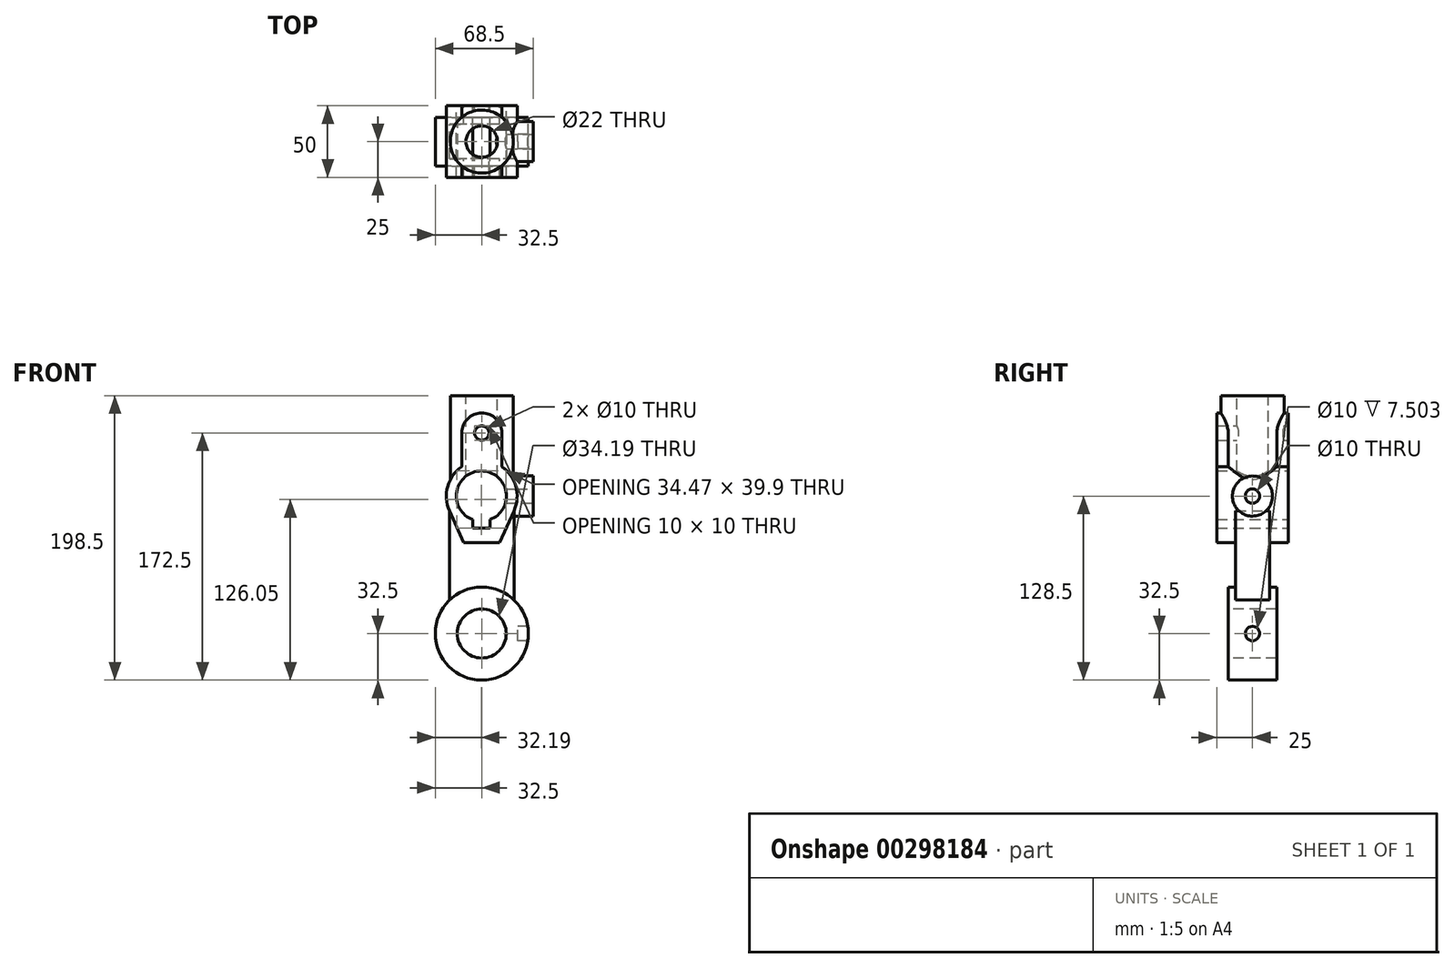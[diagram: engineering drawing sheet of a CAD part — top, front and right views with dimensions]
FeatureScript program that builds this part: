
annotation { "Feature Type Name" : "Feature", "Feature Type Description" : "" }
export const myFeature = defineFeature(function(context is Context, id is Id, definition is map)
    precondition{}
    {
        {
            var Q0;
            Q0=qCreatedBy(makeId("Front.planeOp"),FACE);
            var sketch = newSketch(context, id + "F0", { "sketchPlane" : qUnion([Q0])});
            skLineSegment(sketch, "E0.bottom", {"start": v(-22.5, 96) * mm, "end": v(22.5, 96) * mm});
            skLineSegment(sketch, "E0.top", {"start": v(-22.5, 0) * mm, "end": v(22.5, 0) * mm});
            skLineSegment(sketch, "E0.left", {"start": v(-22.5, 96) * mm, "end": v(-22.5, 0) * mm});
            skLineSegment(sketch, "E0.right", {"start": v(22.5, 96) * mm, "end": v(22.5, 0) * mm});
            skPoint(sketch, "E1", {"position": v(0, 0) * mm});
            skLineSegment(sketch, "E2", {"start": v(0, 0) * mm, "end": v(0, -10.14) * mm, "construction": true});
            skSolve(sketch);
        }
        {
            var Q0;
            Q0 = qSketchRegion(id + "F0", true);
            extrude(context, id + "F1", {"entities" : qUnion([Q0]), "endBound" : BoundingType.SYMMETRIC, "depth" : 24 * mm});
        }
        {
            var Q0;
            Q0=qCreatedBy(makeId("Front.planeOp"),FACE);
            var sketch = newSketch(context, id + "F2", { "sketchPlane" : qUnion([Q0])});
            skCircle(sketch, "E3", {"center": v(0, 0) * mm, "radius": 32.5 * mm});
            skSolve(sketch);
        }
        {
            var Q0;
            Q0 = qSketchRegion(id + "F2", true);
            extrude(context, id + "F3", {"entities" : qUnion([Q0]), "operationType" : NewBodyOperationType.ADD, "endBound" : BoundingType.SYMMETRIC, "depth" : 34 * mm});
        }
        {
            var Q0;
            Q0=qCreatedBy(makeId("Front.planeOp"),FACE);
            var sketch = newSketch(context, id + "F4", { "sketchPlane" : qUnion([Q0])});
            skLineSegment(sketch, "E4", {"start": v(-13.04, 100.57) * mm, "end": v(-13.04, 100.57) * mm});
            skLineSegment(sketch, "E5", {"start": v(0, 0) * mm, "end": v(-53.48, 0) * mm, "construction": true});
            skLineSegment(sketch, "E6", {"start": v(0, 100.39) * mm, "end": v(-0.3, 96) * mm, "construction": true});
            skCircle(sketch, "E7", {"center": v(0, 140) * mm, "radius": 5 * mm});
            skArc(sketch, "E8", {"start": v(-14, 140) * mm, "mid": v(0, 154) * mm, "end": v(14, 140) * mm});
            skArc(sketch, "E9", {"start": v(-6.3, 79.56) * mm, "mid": v(-0.3, 113.5) * mm, "end": v(5.7, 79.56) * mm});
            skLineSegment(sketch, "E10", {"start": v(-6.3, 79.56) * mm, "end": v(-6.3, 73.6) * mm});
            skLineSegment(sketch, "E11", {"start": v(-6.3, 73.6) * mm, "end": v(5.7, 73.6) * mm});
            skLineSegment(sketch, "E12", {"start": v(5.7, 73.6) * mm, "end": v(5.7, 79.56) * mm});
            skLineSegment(sketch, "E13", {"start": v(-12.5, 63.6) * mm, "end": v(12.5, 63.6) * mm});
            skLineSegment(sketch, "E14", {"start": v(-12.5, 63.6) * mm, "end": v(-22.48, 85.72) * mm});
            skLineSegment(sketch, "E15", {"start": v(12.5, 63.6) * mm, "end": v(22.48, 85.72) * mm});
            skLineSegment(sketch, "E16", {"start": v(0, 0) * mm, "end": v(0, -41.14) * mm, "construction": true});
            skArc(sketch, "E17", {"start": v(-22.48, 85.72) * mm, "mid": v(-23.8, 102.64) * mm, "end": v(-14, 116.5) * mm});
            skArc(sketch, "E18", {"start": v(22.48, 85.72) * mm, "mid": v(23.8, 102.64) * mm, "end": v(14, 116.5) * mm});
            skLineSegment(sketch, "E19", {"start": v(-14, 116.5) * mm, "end": v(-14, 140) * mm});
            skLineSegment(sketch, "E20", {"start": v(14, 116.5) * mm, "end": v(14, 140) * mm});
            skSolve(sketch);
        }
        {
            var Q0;
            Q0 = qSketchRegion(id + "F4", true);
            extrude(context, id + "F5", {"entities" : qUnion([Q0]), "operationType" : NewBodyOperationType.ADD, "endBound" : BoundingType.SYMMETRIC, "depth" : 50 * mm});
        }
        {
            var Q0;
            Q0=makeQuery(id+"F3.opExtrude","CAP_FACE",FACE,{"disambiguationData":[OSD([sQuery(id+"F2.wireOp",EDGE,"E3")])],"isStart":false});
            var sketch = newSketch(context, id + "F6", { "sketchPlane" : qUnion([Q0])});
            skCircle(sketch, "E21", {"center": v(0, 0) * mm, "radius": 17.1 * mm});
            skSolve(sketch);
        }
        {
            var Q0;
            Q0 = qSketchRegion(id + "F6", true);
            extrude(context, id + "F7", {"entities" : qUnion([Q0]), "operationType" : NewBodyOperationType.REMOVE, "endBound" : BoundingType.THROUGH_ALL, "oppositeDirection" : true, "depth" : 25 * mm});
        }
        {
            var Q0;
            Q0=qCreatedBy(makeId("Right.planeOp"),FACE);
            var sketch = newSketch(context, id + "F8", { "sketchPlane" : qUnion([Q0])});
            skCircle(sketch, "E22", {"center": v(0, 0) * mm, "radius": 5 * mm});
            skSolve(sketch);
        }
        {
            var Q0;
            Q0 = qSketchRegion(id + "F8", true);
            extrude(context, id + "F9", {"entities" : qUnion([Q0]), "operationType" : NewBodyOperationType.REMOVE, "depth" : 100 * mm, "hasSecondDirection" : true, "secondDirectionOppositeDirection" : false, "secondDirectionDepth" : 25 * mm});
        }
        {
            var Q0;
            Q0=makeQuery(id+"F1.opExtrude","SWEPT_FACE",FACE,{"disambiguationData":[OSD([sQuery(id+"F0.wireOp",EDGE,"E0.bottom")])]});
            var sketch = newSketch(context, id + "F10", { "sketchPlane" : qUnion([Q0])});
            skCircle(sketch, "E23", {"center": v(0, 0) * mm, "radius": 22 * mm});
            skSolve(sketch);
        }
        {
            var Q0;
            Q0 = qSketchRegion(id + "F10", true);
            extrude(context, id + "F11", {"entities" : qUnion([Q0]), "operationType" : NewBodyOperationType.ADD, "depth" : 70 * mm});
        }
        {
            var Q0;
            Q0=makeQuery(id+"F11.opExtrude","CAP_FACE",FACE,{"disambiguationData":[OSD([sQuery(id+"F10.wireOp",EDGE,"E23")])],"isStart":false});
            var sketch = newSketch(context, id + "F12", { "sketchPlane" : qUnion([Q0])});
            skCircle(sketch, "E24", {"center": v(0, 0) * mm, "radius": 11 * mm});
            skSolve(sketch);
        }
        {
            var Q0;
            Q0 = qSketchRegion(id + "F12", true);
            extrude(context, id + "F13", {"entities" : qUnion([Q0]), "operationType" : NewBodyOperationType.REMOVE, "oppositeDirection" : true, "depth" : 60 * mm});
        }
        {
            var Q0;
            Q0=qCreatedBy(makeId("Right.planeOp"),FACE);
            var sketch = newSketch(context, id + "F14", { "sketchPlane" : qUnion([Q0])});
            skLineSegment(sketch, "E25.0.4", {"start": v(-12, 85.77) * mm, "end": v(-12, 85.72) * mm});
            skLineSegment(sketch, "E25.0.6", {"start": v(12, 85.77) * mm, "end": v(12, 85.72) * mm});
            skPoint(sketch, "E25.0.1.start.orphan", {"position": v(-16.97, 116.5) * mm});
            skPoint(sketch, "E25.0.2.start.orphan", {"position": v(-25, 116.5) * mm});
            skPoint(sketch, "E25.0.3.start.orphan", {"position": v(-25, 85.72) * mm});
            skLineSegment(sketch, "E26", {"start": v(0, 0) * mm, "end": v(0, 96) * mm, "construction": true});
            skCircle(sketch, "E27", {"center": v(0, 96) * mm, "radius": 14 * mm});
            skSolve(sketch);
        }
        {
            var Q0;
            Q0 = qSketchRegion(id + "F14", true);
            extrude(context, id + "F15", {"entities" : qUnion([Q0]), "operationType" : NewBodyOperationType.ADD, "depth" : 36 * mm});
        }
        {
            var Q0;
            Q0=makeQuery(id+"F15.opExtrude","CAP_FACE",FACE,{"disambiguationData":[OSD([sQuery(id+"F14.wireOp",EDGE,"E27")])],"isStart":false});
            var sketch = newSketch(context, id + "F16", { "sketchPlane" : qUnion([Q0])});
            skCircle(sketch, "E28", {"center": v(0, 96) * mm, "radius": 5 * mm});
            skSolve(sketch);
        }
        {
            var Q0;
            Q0 = qSketchRegion(id + "F16", true);
            extrude(context, id + "F17", {"entities" : qUnion([Q0]), "operationType" : NewBodyOperationType.REMOVE, "oppositeDirection" : true, "depth" : 25 * mm});
        }
        {
            var Q0;
            Q0=qCreatedBy(makeId("Front.planeOp"),FACE);
            var sketch = newSketch(context, id + "F18", { "sketchPlane" : qUnion([Q0])});
            skCircle(sketch, "E29", {"center": v(-0.3, 96) * mm, "radius": 17.5 * mm});
            skLineSegment(sketch, "E30.bottom", {"start": v(-6.3, 73.6) * mm, "end": v(5.7, 73.6) * mm});
            skLineSegment(sketch, "E30.top", {"start": v(-6.3, 79.56) * mm, "end": v(5.7, 79.56) * mm});
            skLineSegment(sketch, "E30.left", {"start": v(-6.3, 73.6) * mm, "end": v(-6.3, 79.56) * mm});
            skLineSegment(sketch, "E30.right", {"start": v(5.7, 73.6) * mm, "end": v(5.7, 79.56) * mm});
            skPoint(sketch, "E31.0.0.end.orphan", {"position": v(-12.5, 63.6) * mm});
            skPoint(sketch, "E31.0.7.end.orphan", {"position": v(-22.48, 85.72) * mm});
            skPoint(sketch, "E31.0.4.start.orphan", {"position": v(14, 116.5) * mm});
            skPoint(sketch, "E31.0.6.end.orphan", {"position": v(-14, 116.5) * mm});
            skPoint(sketch, "E31.0.2.end.orphan", {"position": v(22.48, 85.72) * mm});
            skPoint(sketch, "E31.0.2.start.orphan", {"position": v(12.5, 63.6) * mm});
            skPoint(sketch, "E31.0.5.end.orphan", {"position": v(-14, 140) * mm});
            skPoint(sketch, "E31.0.5.start.orphan", {"position": v(14, 140) * mm});
            skSolve(sketch);
        }
        {
            var Q0;
            Q0 = qSketchRegion(id + "F18", true);
            extrude(context, id + "F19", {"entities" : qUnion([Q0]), "operationType" : NewBodyOperationType.REMOVE, "endBound" : BoundingType.THROUGH_ALL, "oppositeDirection" : true, "depth" : 25 * mm, "hasSecondDirection" : true, "secondDirectionOppositeDirection" : false, "secondDirectionDepth" : 25 * mm});
        }
        {
            var Q0;
            Q0=qCreatedBy(makeId("Front.planeOp"),FACE);
            var sketch = newSketch(context, id + "F20", { "sketchPlane" : qUnion([Q0])});
            skCircle(sketch, "E32", {"center": v(0, 140) * mm, "radius": 5 * mm});
            skSolve(sketch);
        }
        {
            var Q0;
            Q0 = qSketchRegion(id + "F20", true);
            extrude(context, id + "F21", {"entities" : qUnion([Q0]), "operationType" : NewBodyOperationType.REMOVE, "endBound" : BoundingType.THROUGH_ALL, "depth" : 25 * mm});
        }
    });
